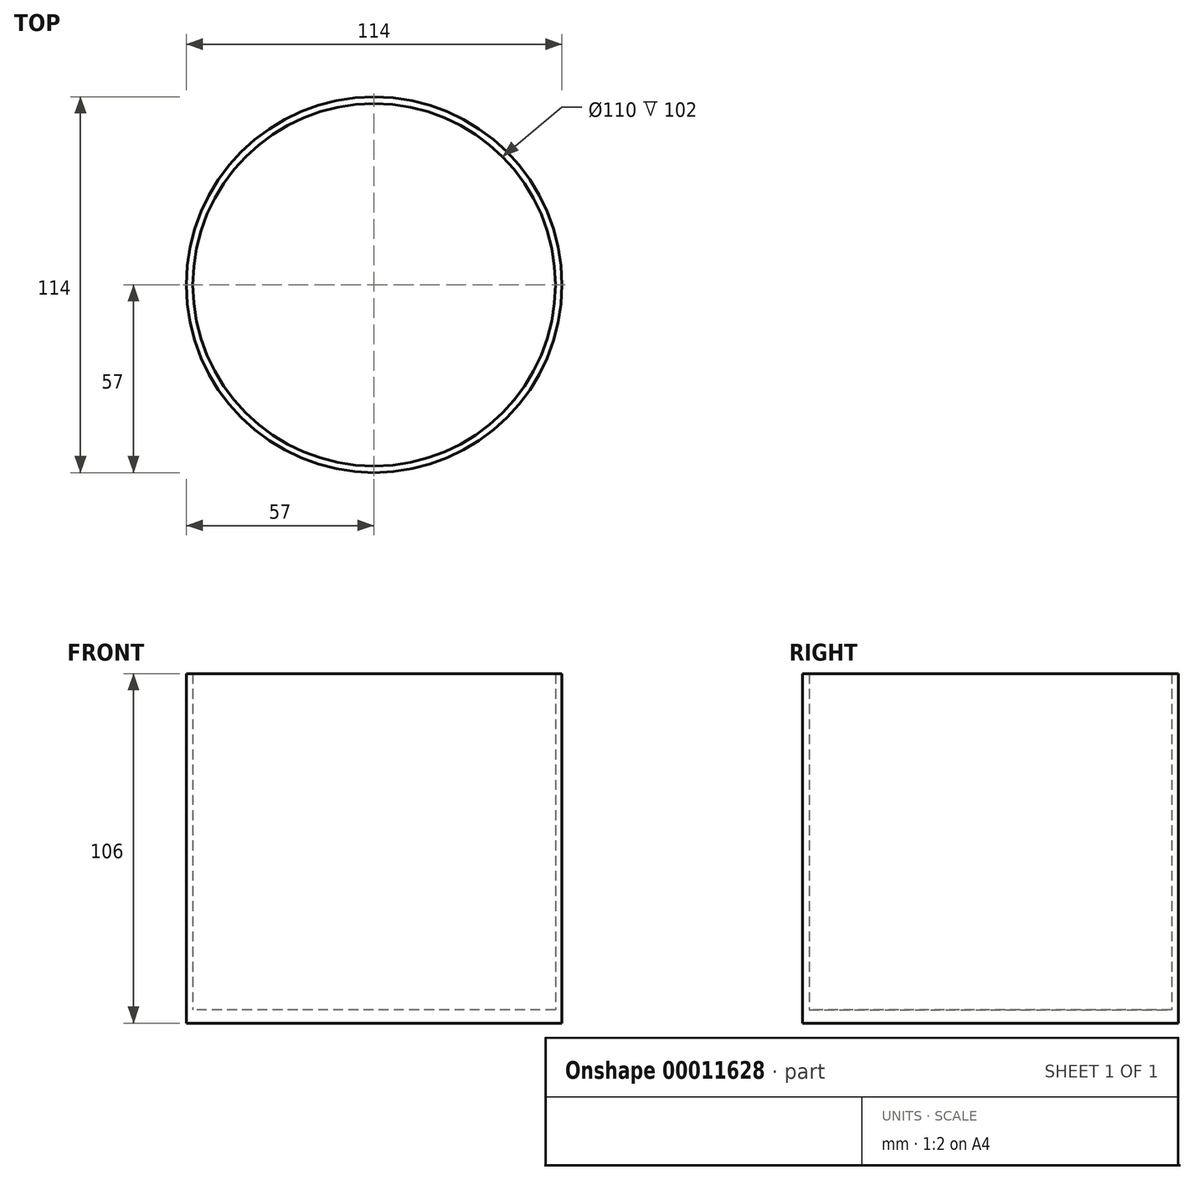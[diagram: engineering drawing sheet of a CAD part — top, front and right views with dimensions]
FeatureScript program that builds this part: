
annotation { "Feature Type Name" : "Feature", "Feature Type Description" : "" }
export const myFeature = defineFeature(function(context is Context, id is Id, definition is map)
    precondition{}
    {
        {
            var Q0;
            Q0=qCreatedBy(makeId("Top.planeOp"),FACE);
            var sketch = newSketch(context, id + "F0", { "sketchPlane" : qUnion([Q0])});
            skCircle(sketch, "E0", {"center": v(0, 0) * mm, "radius": 57 * mm});
            skCircle(sketch, "E1", {"center": v(0, 0) * mm, "radius": 55 * mm});
            skSolve(sketch);
        }
        {
            var Q0;
            Q0 = qSketchRegion(id + "F0", true);
            extrude(context, id + "F1", {"entities" : qUnion([Q0]), "depth" : 102 * mm});
        }
        {
            var Q0;
            Q0=makeQuery(id+"F0.imprint","IMPRINT",FACE,{"disambiguationData":[TD([[makeQuery(id+"F0.imprint","IMPRINT",EDGE,{"derivedFrom":sQuery(id+"F0.wireOp",EDGE,"E1")}),1.0]])]});
            var Q1;
            Q1=makeQuery(id+"F0.imprint","IMPRINT",FACE,{"disambiguationData":[TD([[makeQuery(id+"F0.imprint","IMPRINT",EDGE,{"derivedFrom":sQuery(id+"F0.wireOp",EDGE,"E0")}),1.0]])]});
            extrude(context, id + "F2", {"entities" : qUnion([Q0, Q1]), "operationType" : NewBodyOperationType.ADD, "oppositeDirection" : true, "depth" : 4 * mm});
        }
    });
